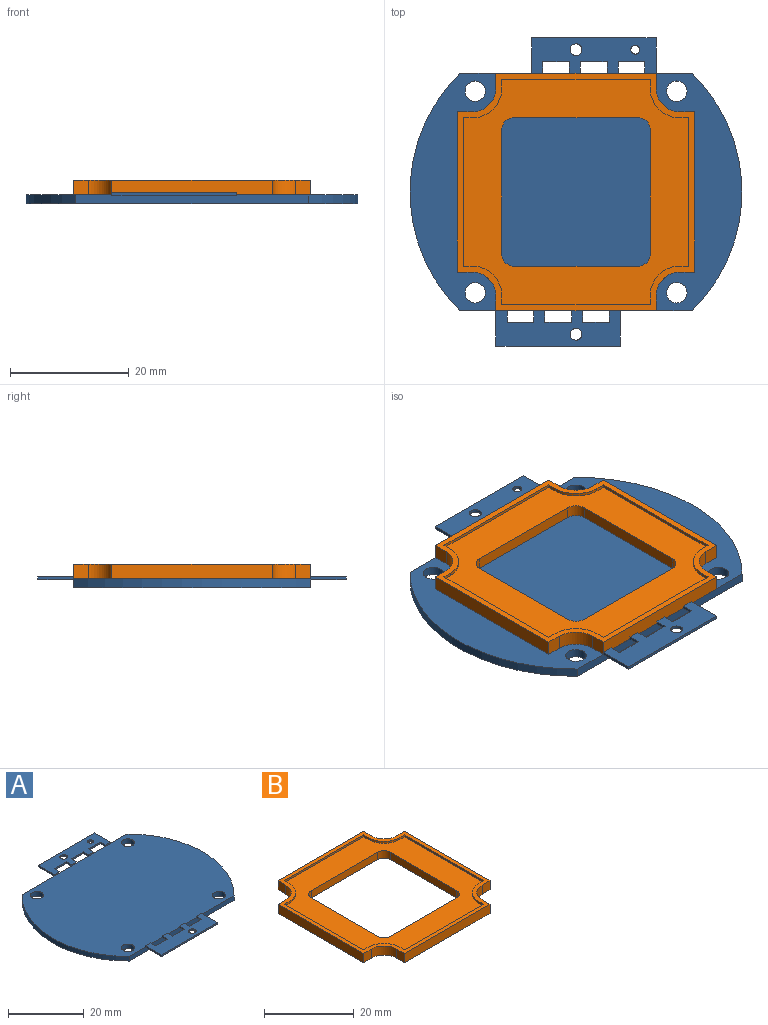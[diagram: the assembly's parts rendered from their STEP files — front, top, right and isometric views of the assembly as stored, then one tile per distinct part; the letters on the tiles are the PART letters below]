
ASSEMBLY  parts=2 mates=1
PART A: 49 faces, bbox 56x52x1.9 mm
  f0: plane 39.19x1.5mm, normal (0,-1,0), area 58mm2, adj f1,f7,f8,f9,f34,f36,f37,f39
  f1: cylinder r=28mm len=40mm, axis (0,0,-1), area 66.8mm2, adj f0,f2,f8,f9
  f2: plane 39.19x1.5mm, normal (0,1,0), area 58mm2, adj f1,f7,f8,f9,f14,f15,f17,f18
  f3: cylinder r=1.72mm len=3.45mm, axis (0,0,-1), area 16.3mm2, adj f8,f9
  f4: cylinder r=1.72mm len=3.45mm, axis (0,0,-1), area 16.3mm2, adj f8,f9
  f5: cylinder r=1.72mm len=3.45mm, axis (0,0,-1), area 16.3mm2, adj f8,f9
  f6: cylinder r=1.72mm len=3.45mm, axis (0,0,-1), area 16.3mm2, adj f8,f9
  f7: cylinder r=28mm len=40mm, axis (0,0,-1), area 66.8mm2, adj f0,f2,f8,f9
  f8: plane 56x40mm, normal (0,0,1), area 1993.9mm2, adj f0,f1,f2,f3,f4,f5,f6,f7
  f9: plane 56x40mm, normal (0,0,-1), area 1993.9mm2, adj f0,f1,f2,f3,f4,f5,f6,f7
  f10: plane 1.88x0.4mm, normal (0,-1,0), area 0.7mm2, adj f8,f14,f15,f28
  f11: plane 1.88x0.4mm, normal (0,-1,0), area 0.7mm2, adj f8,f17,f18,f28
  f12: plane 1.88x0.4mm, normal (0,-1,0), area 0.7mm2, adj f8,f20,f21,f28
  f13: plane 1.88x0.4mm, normal (0,-1,0), area 0.7mm2, adj f8,f23,f24,f28
  f14: plane 2x0.5mm, normal (-1,0,0), area 1mm2, adj f2,f10,f27,f28,f29
  f15: plane 2x0.5mm, normal (1,0,0), area 1mm2, adj f2,f10,f16,f28,f29
  f16: plane 4.5x0.5mm, normal (0,-1,0), area 2.3mm2, adj f15,f17,f28,f29
  f17: plane 2x0.5mm, normal (-1,0,0), area 1mm2, adj f2,f11,f16,f28,f29
  f18: plane 2x0.5mm, normal (1,0,0), area 1mm2, adj f2,f11,f19,f28,f29
  f19: plane 4.5x0.5mm, normal (0,-1,0), area 2.3mm2, adj f18,f20,f28,f29
  f20: plane 2x0.5mm, normal (-1,0,0), area 1mm2, adj f2,f12,f19,f28,f29
  f21: plane 6x0.5mm, normal (1,0,0), area 3mm2, adj f2,f12,f22,f28,f29
  f22: plane 21x0.5mm, normal (0,1,0), area 10.5mm2, adj f21,f23,f28,f29
  f23: plane 6x0.5mm, normal (-1,0,0), area 3mm2, adj f2,f13,f22,f28,f29
  f24: plane 2x0.5mm, normal (1,0,0), area 1mm2, adj f2,f13,f27,f28,f29
  f25: cylinder r=1mm len=2mm, axis (0,0,-1), area 3.1mm2, adj f28,f29
  f26: cylinder r=0.75mm len=1.5mm, axis (0,0,-1), area 2.4mm2, adj f28,f29
  f27: plane 4.5x0.5mm, normal (0,-1,0), area 2.3mm2, adj f14,f24,f28,f29
  f28: plane 21x6mm, normal (0,0,1), area 94.1mm2, adj f10,f11,f12,f13,f14,f15,f16,f17
  f29: plane 21x6mm, normal (0,0,-1), area 94.1mm2, adj f2,f14,f15,f16,f17,f18,f19,f20
  f30: plane 1.88x0.4mm, normal (0,1,0), area 0.7mm2, adj f8,f34,f46,f47
  f31: plane 1.88x0.4mm, normal (0,1,0), area 0.7mm2, adj f8,f36,f37,f47
  f32: plane 1.88x0.4mm, normal (0,1,0), area 0.7mm2, adj f8,f39,f40,f47
  f33: plane 1.88x0.4mm, normal (0,1,0), area 0.7mm2, adj f8,f42,f43,f47
  f34: plane 2x0.5mm, normal (-1,0,0), area 1mm2, adj f0,f30,f35,f47,f48
  f35: plane 4.5x0.5mm, normal (0,1,0), area 2.2mm2, adj f34,f36,f47,f48
  f36: plane 2x0.5mm, normal (1,0,0), area 1mm2, adj f0,f31,f35,f47,f48
  f37: plane 2x0.5mm, normal (-1,0,0), area 1mm2, adj f0,f31,f38,f47,f48
  f38: plane 4.5x0.5mm, normal (0,1,0), area 2.3mm2, adj f37,f39,f47,f48
  f39: plane 2x0.5mm, normal (1,0,0), area 1mm2, adj f0,f32,f38,f47,f48
  f40: plane 2x0.5mm, normal (-1,0,0), area 1mm2, adj f0,f32,f41,f47,f48
  f41: plane 4.5x0.5mm, normal (0,1,0), area 2.2mm2, adj f40,f42,f47,f48
  f42: plane 2x0.5mm, normal (1,0,0), area 1mm2, adj f0,f33,f41,f47,f48
  f43: plane 6x0.5mm, normal (-1,0,0), area 3mm2, adj f0,f33,f44,f47,f48
  f44: plane 21x0.5mm, normal (0,-1,0), area 10.5mm2, adj f43,f46,f47,f48
  f45: cylinder r=1mm len=2mm, axis (0,0,-1), area 3.1mm2, adj f47,f48
  f46: plane 6x0.5mm, normal (1,0,0), area 3mm2, adj f0,f30,f44,f47,f48
  f47: plane 21x6mm, normal (0,0,1), area 95.9mm2, adj f30,f31,f32,f33,f34,f35,f36,f37
  f48: plane 21x6mm, normal (0,0,-1), area 95.9mm2, adj f0,f34,f35,f36,f37,f38,f39,f40
PART B: 43 faces, bbox 40x40x2.5 mm
  f0: plane 21x2mm, normal (0,1,0), area 42mm2, adj f4,f5,f25,f42
  f1: plane 21x2mm, normal (1,0,0), area 42mm2, adj f5,f6,f25,f42
  f2: plane 21x2mm, normal (0,-1,0), area 42mm2, adj f6,f7,f25,f42
  f3: plane 21x2mm, normal (-1,0,0), area 42mm2, adj f4,f7,f25,f42
  f4: cylinder r=2mm len=2mm, axis (0,0,-1), area 6.3mm2, adj f0,f3,f25,f42
  f5: cylinder r=2mm len=2mm, axis (0,0,-1), area 6.3mm2, adj f0,f1,f25,f42
  f6: cylinder r=2mm len=2mm, axis (0,0,-1), area 6.3mm2, adj f1,f2,f25,f42
  f7: cylinder r=2mm len=2mm, axis (0,0,-1), area 6.3mm2, adj f2,f3,f25,f42
  f8: plane 40x40mm, normal (0,0,1), area 148.3mm2, adj f9,f10,f11,f12,f13,f14,f15,f16
  f9: plane 2.5x2.5mm, normal (-1,0,0), area 6.2mm2, adj f8,f10,f24,f25
  f10: plane 27x2.5mm, normal (0,-1,0), area 67.5mm2, adj f8,f9,f11,f25
  f11: plane 2.5x2.5mm, normal (1,0,0), area 6.2mm2, adj f8,f10,f12,f25
  f12: cylinder r=4mm len=4mm, axis (0,0,-1), area 15.7mm2, adj f8,f11,f13,f25
  f13: plane 2.5x2.5mm, normal (0,-1,0), area 6.2mm2, adj f8,f12,f14,f25
  f14: plane 27x2.5mm, normal (1,0,0), area 67.5mm2, adj f8,f13,f15,f25
  f15: plane 2.5x2.5mm, normal (0,1,0), area 6.2mm2, adj f8,f14,f16,f25
  f16: cylinder r=4mm len=4mm, axis (0,0,-1), area 15.7mm2, adj f8,f15,f17,f25
  f17: plane 2.5x2.5mm, normal (1,0,0), area 6.2mm2, adj f8,f16,f18,f25
  f18: plane 27x2.5mm, normal (0,1,0), area 67.5mm2, adj f8,f17,f19,f25
  f19: plane 2.5x2.5mm, normal (-1,0,0), area 6.2mm2, adj f8,f18,f20,f25
  f20: cylinder r=4mm len=4mm, axis (0,0,-1), area 15.7mm2, adj f8,f19,f21,f25
  f21: plane 2.5x2.5mm, normal (0,1,0), area 6.2mm2, adj f8,f20,f22,f25
  f22: plane 27x2.5mm, normal (-1,0,0), area 67.5mm2, adj f8,f21,f23,f25
  f23: plane 2.5x2.5mm, normal (0,-1,0), area 6.2mm2, adj f8,f22,f24,f25
  f24: cylinder r=4mm len=4mm, axis (0,0,-1), area 15.7mm2, adj f8,f9,f23,f25
  f25: plane 40x40mm, normal (0,0,-1), area 823.2mm2, adj f0,f1,f2,f3,f4,f5,f6,f7
  f26: cylinder r=5mm len=5mm, axis (0,0,1), area 3.9mm2, adj f8,f27,f41,f42
  f27: plane 1.5x0.5mm, normal (0,1,0), area 0.7mm2, adj f8,f26,f28,f42
  f28: plane 25x0.5mm, normal (-1,0,0), area 12.5mm2, adj f8,f27,f29,f42
  f29: plane 1.5x0.5mm, normal (0,-1,0), area 0.7mm2, adj f8,f28,f30,f42
  f30: cylinder r=5mm len=5mm, axis (0,0,1), area 3.9mm2, adj f8,f29,f31,f42
  f31: plane 1.5x0.5mm, normal (-1,0,0), area 0.7mm2, adj f8,f30,f32,f42
  f32: plane 25x0.5mm, normal (0,-1,0), area 12.5mm2, adj f8,f31,f33,f42
  f33: plane 1.5x0.5mm, normal (1,0,0), area 0.7mm2, adj f8,f32,f34,f42
  f34: cylinder r=5mm len=5mm, axis (0,0,1), area 3.9mm2, adj f8,f33,f35,f42
  f35: plane 1.5x0.5mm, normal (0,-1,0), area 0.7mm2, adj f8,f34,f36,f42
  f36: plane 25x0.5mm, normal (1,0,0), area 12.5mm2, adj f8,f35,f37,f42
  f37: plane 1.5x0.5mm, normal (0,1,0), area 0.7mm2, adj f8,f36,f38,f42
  f38: cylinder r=5mm len=5mm, axis (0,0,1), area 3.9mm2, adj f8,f37,f39,f42
  f39: plane 1.5x0.5mm, normal (1,0,0), area 0.7mm2, adj f8,f38,f40,f42
  f40: plane 25x0.5mm, normal (0,1,0), area 12.5mm2, adj f8,f39,f41,f42
  f41: plane 1.5x0.5mm, normal (-1,0,0), area 0.7mm2, adj f8,f26,f40,f42
  f42: plane 38x38mm, normal (0,0,1), area 674.9mm2, adj f0,f1,f2,f3,f4,f5,f6,f7
PLACE A at identity
PLACE B at identity
MATE fastened B.f42 <-> A.f1  axis (0,0,1) through (0,0,3.5)mm
